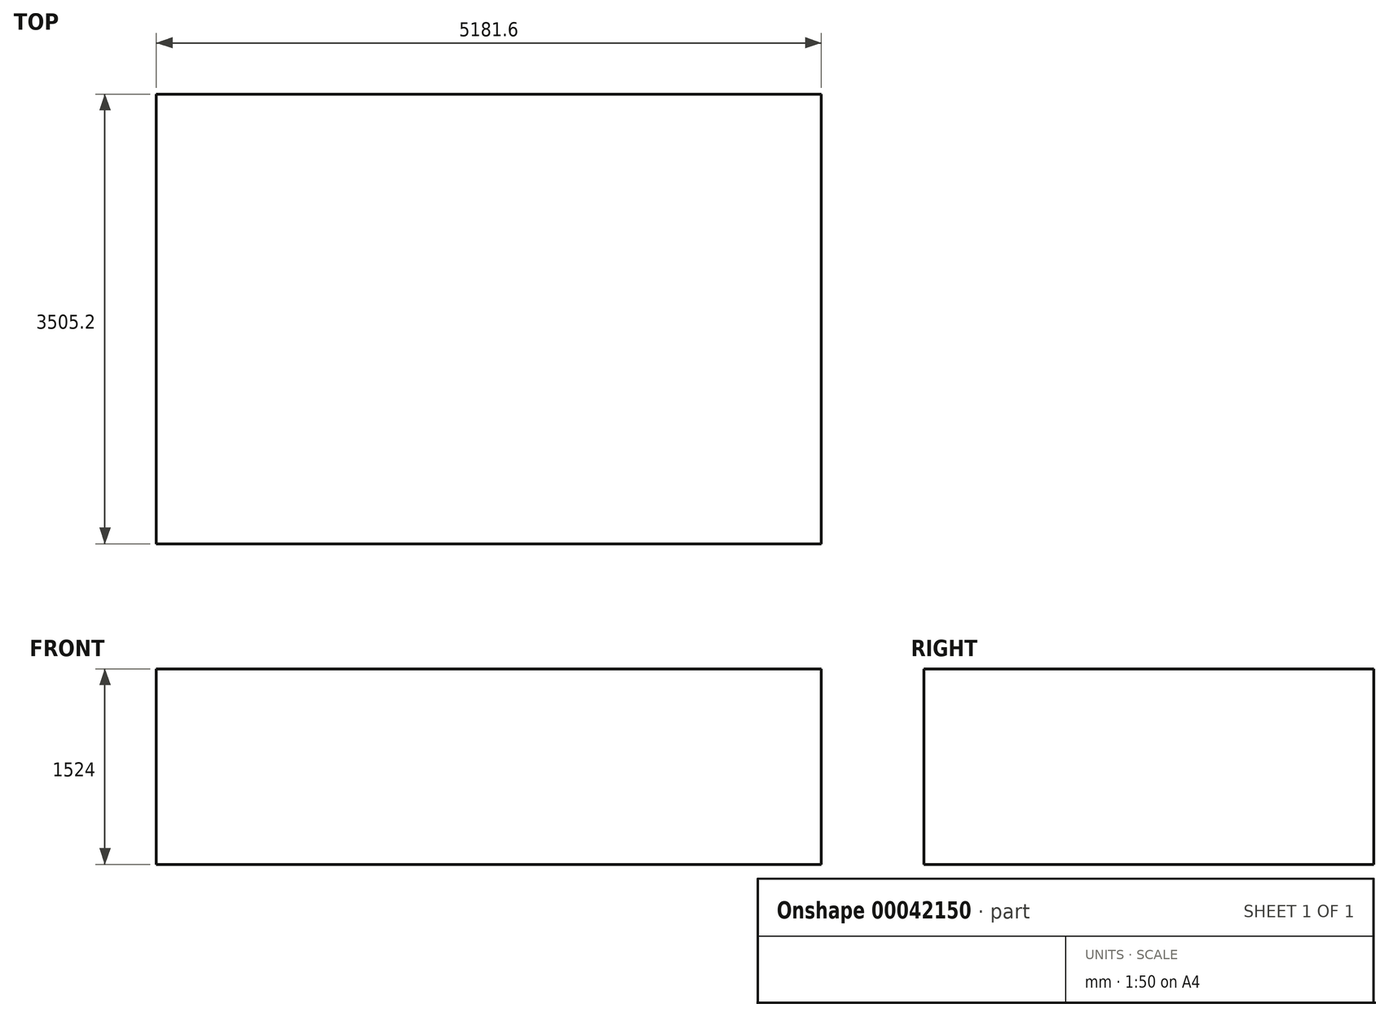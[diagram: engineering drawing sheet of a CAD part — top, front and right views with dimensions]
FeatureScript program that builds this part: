
annotation { "Feature Type Name" : "Feature", "Feature Type Description" : "" }
export const myFeature = defineFeature(function(context is Context, id is Id, definition is map)
    precondition{}
    {
        {
            var Q0;
            Q0=qCreatedBy(makeId("Top.planeOp"),FACE);
            var sketch = newSketch(context, id + "F0", { "sketchPlane" : qUnion([Q0])});
            skLineSegment(sketch, "E0.bottom", {"start": v(0, 0) * mm, "end": v(5181.6, 0) * mm});
            skLineSegment(sketch, "E0.top", {"start": v(0, 3505.2) * mm, "end": v(5181.6, 3505.2) * mm});
            skLineSegment(sketch, "E0.left", {"start": v(0, 0) * mm, "end": v(0, 3505.2) * mm});
            skLineSegment(sketch, "E0.right", {"start": v(5181.6, 0) * mm, "end": v(5181.6, 3505.2) * mm});
            skSolve(sketch);
        }
        {
            var Q0;
            Q0 = qSketchRegion(id + "F0", true);
            extrude(context, id + "F1", {"entities" : qUnion([Q0]), "depth" : 1524 * mm});
        }
    });
